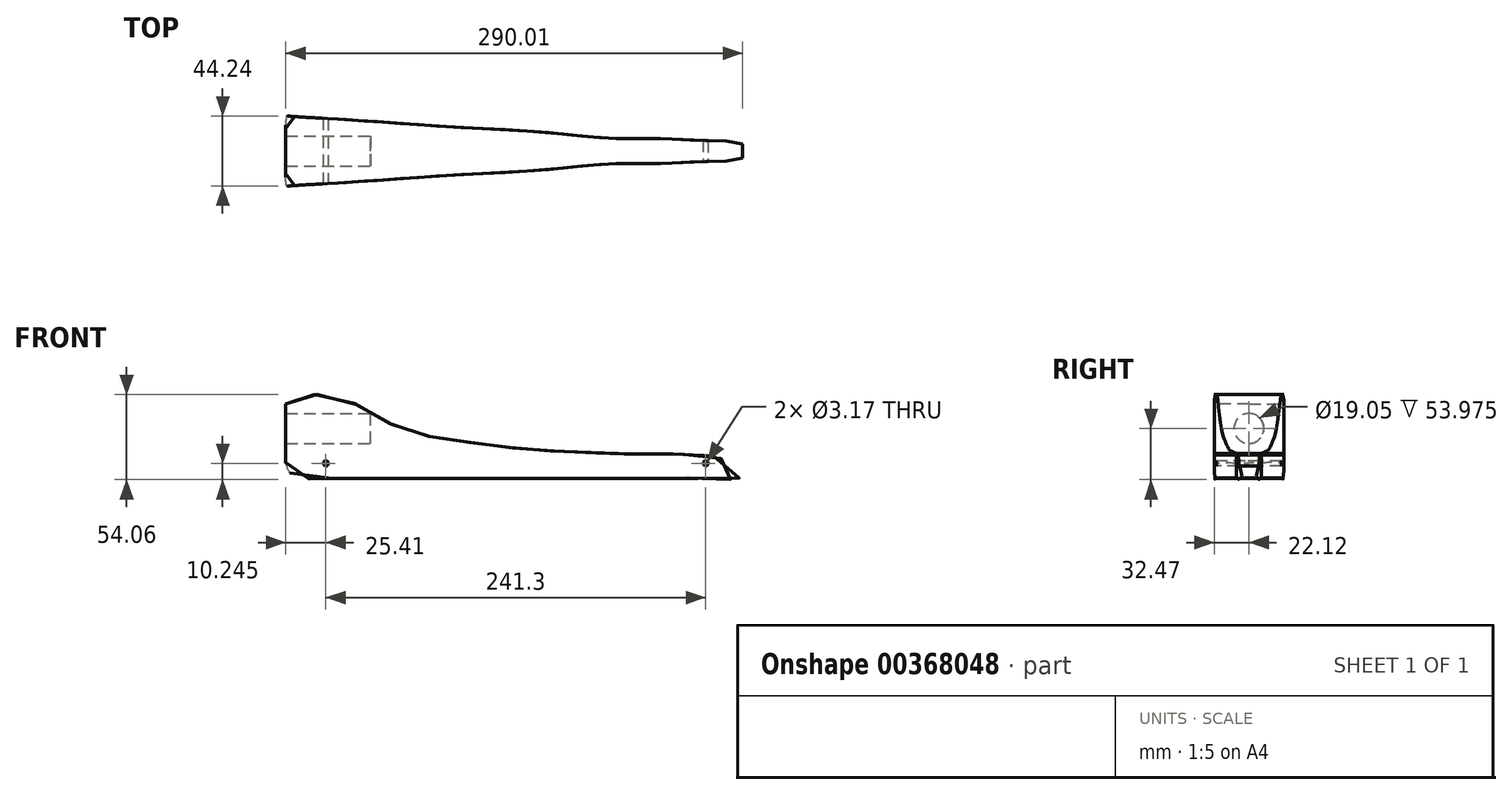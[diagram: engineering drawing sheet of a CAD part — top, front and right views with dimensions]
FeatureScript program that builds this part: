
annotation { "Feature Type Name" : "Feature", "Feature Type Description" : "" }
export const myFeature = defineFeature(function(context is Context, id is Id, definition is map)
    precondition{}
    {
        {
            var Q0;
            Q0=qCreatedBy(makeId("Front.planeOp"),FACE);
            var sketch = newSketch(context, id + "F0", { "sketchPlane" : qUnion([Q0])});
            skLineSegment(sketch, "E0.bottom", {"start": v(-147.87, 31.75) * mm, "end": v(144.23, 31.75) * mm, "construction": true});
            skLineSegment(sketch, "E0.top", {"start": v(-147.87, -31.75) * mm, "end": v(144.23, -31.75) * mm, "construction": true});
            skLineSegment(sketch, "E0.right", {"start": v(144.23, 31.75) * mm, "end": v(144.23, -31.75) * mm, "construction": true});
            skFitSpline(sketch, "E1", {"points": [v(-147.87, -7.12) * mm, v(-147.87, 0) * mm, v(-145.82, 15.9) * mm, v(-135.09, 20.94) * mm, v(-121.3, 21.44) * mm, v(-107.6, 18.35) * mm, v(-90.03, 8.58) * mm, v(-66.18, -2.41) * mm, v(-34.73, -8.2) * mm, v(11.49, -13.5) * mm, v(62.46, -15.79) * mm, v(87.26, -16.7) * mm, v(98.5, -16.44) * mm, v(128.8, -18.5) * mm, v(143.78, -30.26) * mm, v(115.46, -31.75) * mm, v(90.9, -31.75) * mm, v(68.3, -31.75) * mm, v(46.6, -31.75) * mm, v(19.15, -31.75) * mm, v(-6.92, -31.75) * mm, v(-28.11, -31.75) * mm, v(-58.89, -31.75) * mm, v(-90.48, -31.75) * mm, v(-109.95, -31.74) * mm, v(-128.25, -31.75) * mm, v(-142.44, -29.68) * mm, v(-147.87, -7.12) * mm]});
            skLineSegment(sketch, "E2.bottom", {"start": v(-147.87, 9.52) * mm, "end": v(-97.08, 9.52) * mm, "construction": true});
            skLineSegment(sketch, "E2.top", {"start": v(-141.83, -9.52) * mm, "end": v(-97.07, -9.52) * mm, "construction": true});
            skLineSegment(sketch, "E2.right", {"start": v(-97.07, 9.53) * mm, "end": v(-97.07, -9.52) * mm, "construction": true});
            skLineSegment(sketch, "E3", {"start": v(-147.87, 31.75) * mm, "end": v(-147.87, -31.75) * mm, "construction": true});
            skSolve(sketch);
        }
        {
            var Q0;
            Q0=qCreatedBy(makeId("Top.planeOp"),FACE);
            var sketch = newSketch(context, id + "F1", { "sketchPlane" : qUnion([Q0])});
            skLineSegment(sketch, "E4.bottom", {"start": v(-146.05, 22.22) * mm, "end": v(146.05, 22.23) * mm, "construction": true});
            skLineSegment(sketch, "E4.top", {"start": v(-146.05, -22.23) * mm, "end": v(146.05, -22.22) * mm, "construction": true});
            skLineSegment(sketch, "E4.left", {"start": v(-146.05, 22.22) * mm, "end": v(-146.05, -22.23) * mm, "construction": true});
            skLineSegment(sketch, "E4.right", {"start": v(146.05, 22.22) * mm, "end": v(146.05, -22.22) * mm, "construction": true});
            skLineSegment(sketch, "E5", {"start": v(-146.05, 0) * mm, "end": v(146.05, 0) * mm, "construction": true});
            skFitSpline(sketch, "E6", {"points": [v(-146.05, 0) * mm, v(-146.04, 20) * mm, v(-145.68, 21.83) * mm, v(-141.76, 21.98) * mm, v(-92.76, 18.94) * mm, v(-46.84, 15.73) * mm, v(-5.04, 13.43) * mm, v(27.1, 11.14) * mm, v(63.38, 7.92) * mm, v(86.66, 7.91) * mm, v(105.15, 7.23) * mm, v(131.17, 6.54) * mm, v(146.05, 0) * mm], "startDerivative": vector(0, 335.54) * mm, "endDerivative": vector(0.14, -277.48) * mm});
            skFitSpline(sketch, "E7.MirrorCS", {"points": [v(-146.05, 0) * mm, v(-146.04, -20) * mm, v(-145.68, -21.83) * mm, v(-141.76, -21.98) * mm, v(-92.76, -18.94) * mm, v(-46.84, -15.73) * mm, v(-5.04, -13.43) * mm, v(27.1, -11.14) * mm, v(63.38, -7.92) * mm, v(86.66, -7.91) * mm, v(105.15, -7.23) * mm, v(131.17, -6.54) * mm, v(146.05, 0) * mm], "startDerivative": vector(0, -335.54) * mm, "endDerivative": vector(0.14, 277.48) * mm});
            skLineSegment(sketch, "E8.MirrorCS", {"start": v(-146.05, -22.23) * mm, "end": v(146.05, -22.23) * mm});
            skSolve(sketch);
        }
        {
            var Q0;
            Q0=qCreatedBy(makeId("Right.planeOp"),FACE);
            var sketch = newSketch(context, id + "F2", { "sketchPlane" : qUnion([Q0])});
            skCircle(sketch, "E9", {"center": v(0, 0) * mm, "radius": 9.53 * mm});
            skSolve(sketch);
        }
        {
            var Q0;
            Q0=qCreatedBy(makeId("Front.planeOp"),FACE);
            var sketch = newSketch(context, id + "F3", { "sketchPlane" : qUnion([Q0])});
            skCircle(sketch, "E10", {"center": v(-120.65, -22.22) * mm, "radius": 1.59 * mm});
            skCircle(sketch, "E11", {"center": v(120.65, -22.23) * mm, "radius": 1.59 * mm});
            skSolve(sketch);
        }
        {
            var Q0;
            Q0=qSketchRegion(id+"F0",true);
            extrude(context, id + "F4", {"entities" : qUnion([Q0]), "depth" : 44.45 * mm, "symmetric" : true});
        }
        {
            var Q0;
            Q0=qSketchRegion(id+"F1",true);
            extrude(context, id + "F5", {"entities" : qUnion([Q0]), "operationType" : NewBodyOperationType.INTERSECT, "endBound" : BoundingType.THROUGH_ALL, "oppositeDirection" : true, "depth" : 60.96 * mm, "hasSecondDirection" : true, "secondDirectionBound" : BoundingType.THROUGH_ALL, "secondDirectionOppositeDirection" : false, "secondDirectionDepth" : 25.4 * mm});
        }
        {
            var Q0;
            Q0=qSketchRegion(id+"F2",true);
            extrude(context, id + "F6", {"entities" : qUnion([Q0]), "operationType" : NewBodyOperationType.REMOVE, "oppositeDirection" : true, "depth" : 152.4 * mm, "hasSecondDirection" : true, "secondDirectionOppositeDirection" : true, "secondDirectionDepth" : 92.07 * mm});
        }
        {
            var Q0;
            Q0=qSketchRegion(id+"F3",true);
            extrude(context, id + "F7", {"entities" : qUnion([Q0]), "operationType" : NewBodyOperationType.REMOVE, "oppositeDirection" : true, "depth" : 50.8 * mm, "symmetric" : true});
        }
    });
